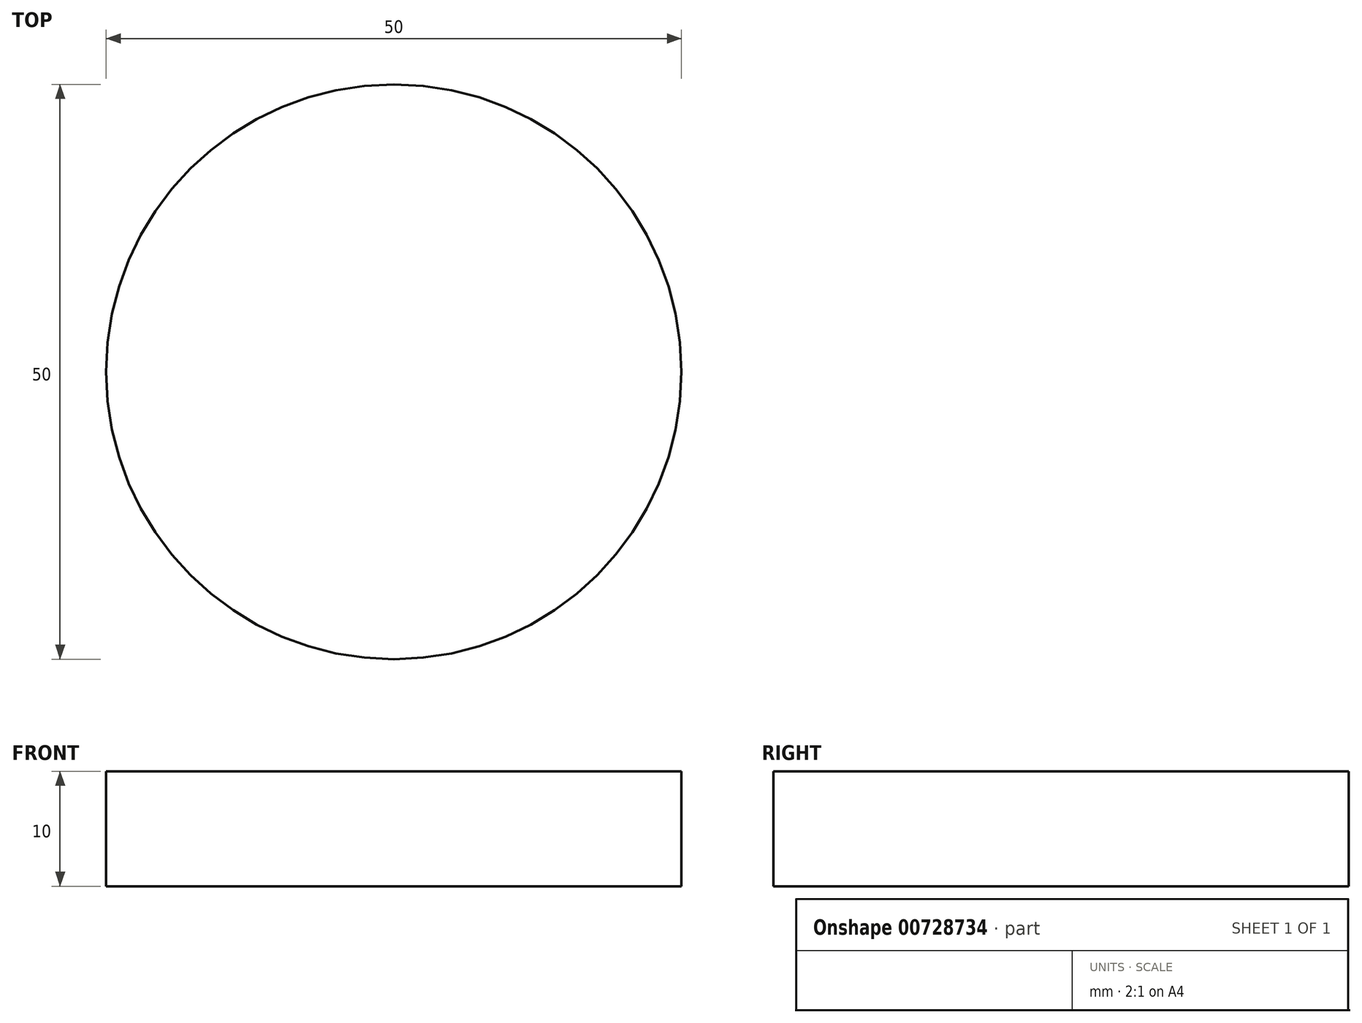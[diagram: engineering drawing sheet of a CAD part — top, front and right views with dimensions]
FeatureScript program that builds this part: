
annotation { "Feature Type Name" : "Feature", "Feature Type Description" : "" }
export const myFeature = defineFeature(function(context is Context, id is Id, definition is map)
    precondition{}
    {
        {
            var Q0;
            Q0=qCreatedBy(makeId("Top.planeOp"),FACE);
            var sketch = newSketch(context, id + "F0", { "sketchPlane" : qUnion([Q0])});
            skCircle(sketch, "E0", {"center": v(0, 0) * mm, "radius": 25 * mm});
            skLineSegment(sketch, "E1", {"start": v(72.23, 0) * mm, "end": v(-64.06, 0) * mm, "construction": true});
            skLineSegment(sketch, "E2", {"start": v(0, 62.8) * mm, "end": v(0, -65) * mm, "construction": true});
            skCircle(sketch, "E3", {"center": v(0, 25) * mm, "radius": 10 * mm});
            skCircle(sketch, "E4", {"center": v(-9.8, 23) * mm, "radius": 10 * mm});
            skSolve(sketch);
        }
        {
            var Q0;
            {var subQ0=sQuery(id+"F0.wireOp",EDGE,"E4");var subQ1=sQuery(id+"F0.wireOp",EDGE,"E0");var subQ2=makeQuery(id+"F0.imprint","INTERSECT",VERTEX,{"disambiguationData":[OD(0.0)],"derivedFrom":[subQ1,subQ0]});Q0=makeQuery(id+"F0.imprint","IMPRINT",FACE,{"disambiguationData":[TD([[makeQuery(id+"F0.imprint","IMPRINT",EDGE,{"disambiguationData":[TD([[subQ2,1.0]])],"derivedFrom":subQ1}),1.0]])]});}
            var Q1;
            {var subQ0=sQuery(id+"F0.wireOp",EDGE,"E3");var subQ1=sQuery(id+"F0.wireOp",EDGE,"E0");var subQ2=makeQuery(id+"F0.imprint","INTERSECT",VERTEX,{"disambiguationData":[OD(0.0)],"derivedFrom":[subQ1,subQ0]});Q1=makeQuery(id+"F0.imprint","IMPRINT",FACE,{"disambiguationData":[TD([[makeQuery(id+"F0.imprint","IMPRINT",EDGE,{"disambiguationData":[TD([[subQ2,-1.0]])],"derivedFrom":subQ1}),1.0]])]});}
            var Q2;
            {var subQ0=sQuery(id+"F0.wireOp",EDGE,"E4");var subQ1=sQuery(id+"F0.wireOp",EDGE,"E0");var subQ2=makeQuery(id+"F0.imprint","INTERSECT",VERTEX,{"disambiguationData":[OD(1.0)],"derivedFrom":[subQ1,subQ0]});Q2=makeQuery(id+"F0.imprint","IMPRINT",FACE,{"disambiguationData":[TD([[makeQuery(id+"F0.imprint","IMPRINT",EDGE,{"disambiguationData":[TD([[subQ2,-1.0]])],"derivedFrom":subQ1}),1.0]])]});}
            var Q3;
            {var subQ0=sQuery(id+"F0.wireOp",EDGE,"E3");var subQ1=sQuery(id+"F0.wireOp",EDGE,"E0");var subQ2=makeQuery(id+"F0.imprint","INTERSECT",VERTEX,{"disambiguationData":[OD(0.0)],"derivedFrom":[subQ1,subQ0]});Q3=makeQuery(id+"F0.imprint","IMPRINT",FACE,{"disambiguationData":[TD([[makeQuery(id+"F0.imprint","IMPRINT",EDGE,{"disambiguationData":[TD([[subQ2,1.0]])],"derivedFrom":subQ1}),1.0]])]});}
            extrude(context, id + "F1", {"entities" : qUnion([Q0, Q1, Q2, Q3]), "depth" : 10 * mm, "offsetDistance" : 25 * mm});
        }
    });
